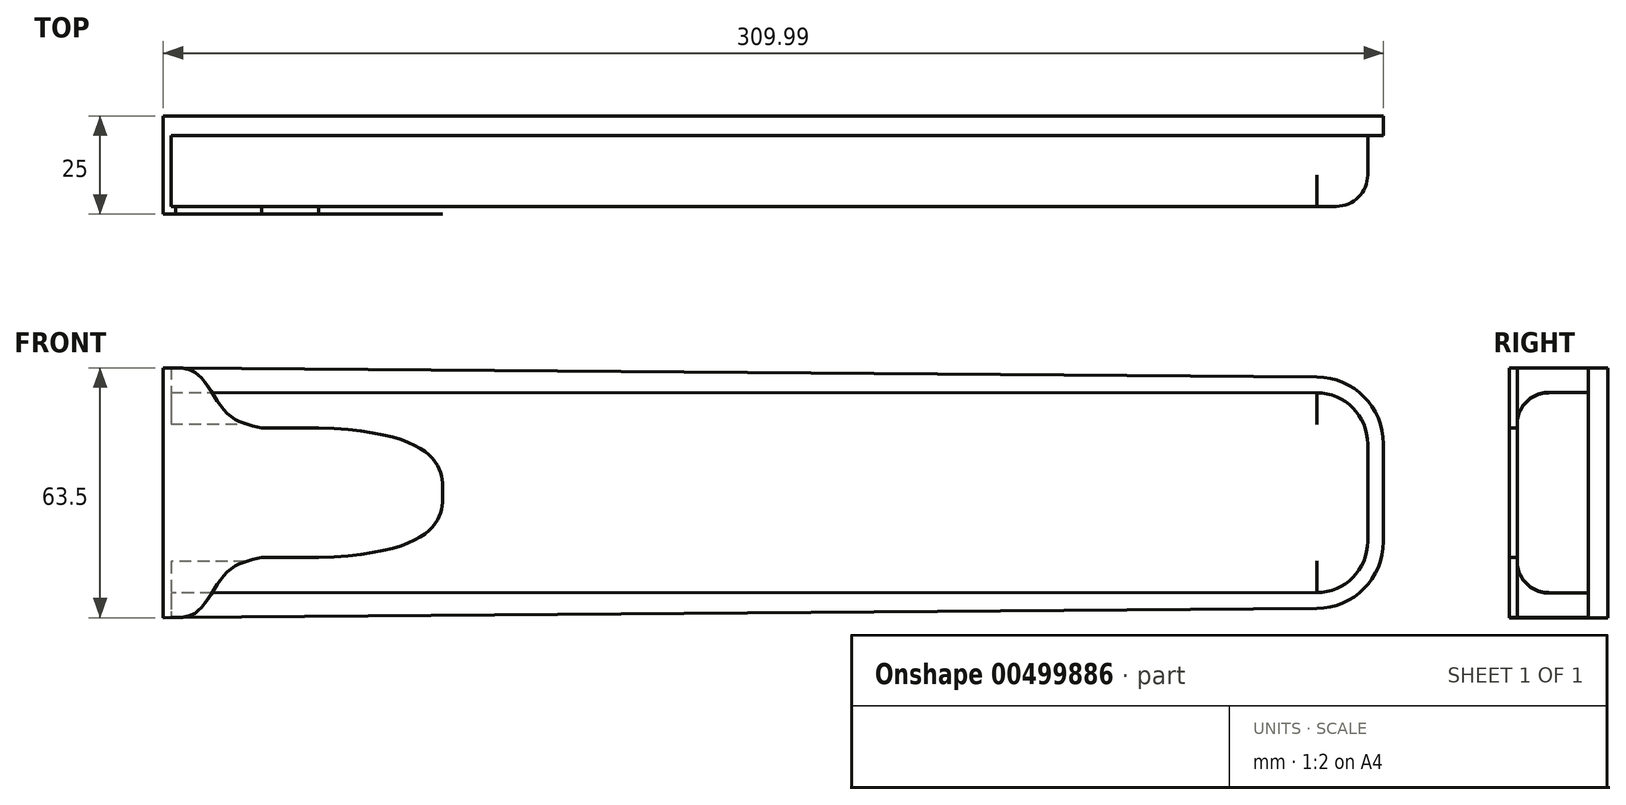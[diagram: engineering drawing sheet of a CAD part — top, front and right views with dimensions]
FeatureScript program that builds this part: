
annotation { "Feature Type Name" : "Feature", "Feature Type Description" : "" }
export const myFeature = defineFeature(function(context is Context, id is Id, definition is map)
    precondition{}
    {
        {
            var Q0;
            Q0=qCreatedBy(makeId("Front.planeOp"),FACE);
            var sketch = newSketch(context, id + "F0", { "sketchPlane" : qUnion([Q0])});
            skPoint(sketch, "E0.middle", {"position": v(0, 0) * mm});
            skLineSegment(sketch, "E1", {"start": v(-136.9, -2.5) * mm, "end": v(156.22, -0.14) * mm});
            skLineSegment(sketch, "E2", {"start": v(173.08, 16.86) * mm, "end": v(173.08, 41.64) * mm});
            skLineSegment(sketch, "E3", {"start": v(156.22, 58.64) * mm, "end": v(-136.9, 61) * mm});
            skLineSegment(sketch, "E4", {"start": v(-136.9, 61) * mm, "end": v(-136.9, -2.5) * mm});
            skPoint(sketch, "E5.visualSharp", {"position": v(173.08, 58.5) * mm});
            skArc(sketch, "E5.filletArc", {"start": v(173.08, 41.64) * mm, "mid": v(168.15, 53.6) * mm, "end": v(156.22, 58.64) * mm});
            skPoint(sketch, "E6.visualSharp", {"position": v(173.08, 0) * mm});
            skArc(sketch, "E6.filletArc", {"start": v(156.22, -0.14) * mm, "mid": v(168.15, 4.9) * mm, "end": v(173.08, 16.86) * mm});
            skSolve(sketch);
        }
        {
            var Q0;
            Q0=makeQuery(id+"F0.imprint","IMPRINT",FACE,{"disambiguationData":[TD([[makeQuery(id+"F0.imprint","IMPRINT",EDGE,{"derivedFrom":sQuery(id+"F0.wireOp",EDGE,"E1")}),1.0]])]});
            extrude(context, id + "F1", {"entities" : qUnion([Q0]), "depth" : 5 * mm});
        }
        {
            var Q0;
            Q0=makeQuery(id+"F1.opExtrude","CAP_FACE",FACE,{"disambiguationData":[OSD([sQuery(id+"F0.wireOp",EDGE,"E1"),sQuery(id+"F0.wireOp",EDGE,"E2"),sQuery(id+"F0.wireOp",EDGE,"E3"),sQuery(id+"F0.wireOp",EDGE,"E4"),sQuery(id+"F0.wireOp",EDGE,"E5.filletArc"),sQuery(id+"F0.wireOp",EDGE,"E6.filletArc")])],"isStart":false});
            var sketch = newSketch(context, id + "F2", { "sketchPlane" : qUnion([Q0])});
            skArc(sketch, "E7.0", {"start": v(169.08, 41.64) * mm, "mid": v(165.3, 50.8) * mm, "end": v(156.18, 54.64) * mm});
            skLineSegment(sketch, "E7.1", {"start": v(169.08, 16.86) * mm, "end": v(169.08, 41.64) * mm});
            skArc(sketch, "E7.2", {"start": v(156.18, 3.86) * mm, "mid": v(165.3, 7.7) * mm, "end": v(169.08, 16.86) * mm});
            skLineSegment(sketch, "E8.0", {"start": v(-134.9, 54.75) * mm, "end": v(-134.9, 3.75) * mm});
            skPoint(sketch, "E9", {"position": v(-134.9, 29.25) * mm});
            skPoint(sketch, "E10", {"position": v(-136.9, 29.25) * mm});
            skLineSegment(sketch, "E11", {"start": v(-134.9, 54.75) * mm, "end": v(156.18, 54.64) * mm});
            skLineSegment(sketch, "E12", {"start": v(156.18, 3.86) * mm, "end": v(-134.9, 3.75) * mm});
            skSolve(sketch);
        }
        {
            var Q0;
            Q0=makeQuery(id+"F2.imprint","IMPRINT",FACE,{"disambiguationData":[TD([[makeQuery(id+"F2.imprint","IMPRINT",EDGE,{"derivedFrom":sQuery(id+"F2.wireOp",EDGE,"E7.0")}),1.0]])]});
            extrude(context, id + "F3", {"entities" : qUnion([Q0]), "operationType" : NewBodyOperationType.ADD, "depth" : 18 * mm});
        }
        {
            var Q0;
            Q0=makeQuery(id+"F3.opExtrude","CAP_EDGE",EDGE,{"disambiguationData":[OSD([sQuery(id+"F2.wireOp",EDGE,"E11")])],"isStart":false});
            var Q1;
            Q1=makeQuery(id+"F3.opExtrude","CAP_EDGE",EDGE,{"disambiguationData":[OSD([sQuery(id+"F2.wireOp",EDGE,"E7.0")])],"isStart":false});
            var Q2;
            Q2=makeQuery(id+"F3.opExtrude","CAP_EDGE",EDGE,{"disambiguationData":[OSD([sQuery(id+"F2.wireOp",EDGE,"E7.1")])],"isStart":false});
            var Q3;
            Q3=makeQuery(id+"F3.opExtrude","CAP_EDGE",EDGE,{"disambiguationData":[OSD([sQuery(id+"F2.wireOp",EDGE,"E7.2")])],"isStart":false});
            var Q4;
            Q4=makeQuery(id+"F3.opExtrude","CAP_EDGE",EDGE,{"disambiguationData":[OSD([sQuery(id+"F2.wireOp",EDGE,"E12")])],"isStart":false});
            fillet(context, id + "F4", {"entities" : qUnion([Q0, Q1, Q2, Q3, Q4]), "radius" : 8 * mm, "tangentPropagation" : true, "allowEdgeOverflow" : false});
        }
        {
            var Q0;
            Q0=makeQuery(id+"F1.opExtrude","CAP_FACE",FACE,{"disambiguationData":[OSD([sQuery(id+"F0.wireOp",EDGE,"E1"),sQuery(id+"F0.wireOp",EDGE,"E2"),sQuery(id+"F0.wireOp",EDGE,"E3"),sQuery(id+"F0.wireOp",EDGE,"E4"),sQuery(id+"F0.wireOp",EDGE,"E5.filletArc"),sQuery(id+"F0.wireOp",EDGE,"E6.filletArc")])],"isStart":false});
            var sketch = newSketch(context, id + "F5", { "sketchPlane" : qUnion([Q0])});
            skLineSegment(sketch, "E13.0", {"start": v(-134.9, 61) * mm, "end": v(-134.9, -2.5) * mm});
            skLineSegment(sketch, "E14", {"start": v(-136.9, -2.5) * mm, "end": v(-134.9, -2.5) * mm});
            skLineSegment(sketch, "E15", {"start": v(-136.9, 61) * mm, "end": v(-134.9, 61) * mm});
            skSolve(sketch);
        }
        {
            var Q0;
            {var subQ0=makeQuery(id+"F1.opExtrude","CAP_EDGE",EDGE,{"disambiguationData":[OSD([sQuery(id+"F0.wireOp",EDGE,"E4")])],"isStart":false});Q0=makeQuery(id+"F5.imprint","IMPRINT",FACE,{"disambiguationData":[TD([[makeQuery(id+"F5.imprint","IMPRINT",EDGE,{"derivedFrom":subQ0}),1.0]])]});}
            extrude(context, id + "F6", {"entities" : qUnion([Q0]), "operationType" : NewBodyOperationType.ADD, "depth" : 20 * mm});
        }
        {
            var Q0;
            Q0=makeQuery(id+"F6.opExtrude","SWEPT_FACE",FACE,{"disambiguationData":[OSD([sQuery(id+"F5.wireOp",EDGE,"E13.0")])]});
            var sketch = newSketch(context, id + "F7", { "sketchPlane" : qUnion([Q0])});
            skLineSegment(sketch, "E16.bottom", {"start": v(-25, -2.48) * mm, "end": v(-23, -2.48) * mm});
            skLineSegment(sketch, "E16.top", {"start": v(-25, 60.98) * mm, "end": v(-23, 60.98) * mm});
            skLineSegment(sketch, "E16.left", {"start": v(-25, -2.48) * mm, "end": v(-25, 60.98) * mm});
            skLineSegment(sketch, "E16.right", {"start": v(-23, -2.48) * mm, "end": v(-23, 60.98) * mm});
            skSolve(sketch);
        }
        {
            var Q0;
            {var subQ3=sQuery(id+"F7.wireOp",EDGE,"E16.bottom");Q0=makeQuery(id+"F7.imprint","IMPRINT",FACE,{"disambiguationData":[TD([[makeQuery(id+"F7.imprint","IMPRINT",EDGE,{"derivedFrom":subQ3}),1.0]])]});}
            extrude(context, id + "F8", {"entities" : qUnion([Q0]), "operationType" : NewBodyOperationType.ADD, "depth" : 69 * mm});
        }
        {
            var Q0;
            Q0=makeQuery(id+"F8.boolean.opBoolean","MERGE",FACE,{"derivedFrom":[makeQuery(id+"F6.opExtrude","CAP_FACE",FACE,{"disambiguationData":[OSD([sQuery(id+"F0.wireOp",EDGE,"E1"),sQuery(id+"F0.wireOp",EDGE,"E3"),sQuery(id+"F0.wireOp",EDGE,"E4"),sQuery(id+"F5.wireOp",EDGE,"E13.0")])],"isStart":false}),makeQuery(id+"F8.opExtrude","SWEPT_FACE",FACE,{"disambiguationData":[OSD([sQuery(id+"F7.wireOp",EDGE,"E16.left")])]})]});
            var sketch = newSketch(context, id + "F9", { "sketchPlane" : qUnion([Q0])});
            skPoint(sketch, "E17", {"position": v(-136.9, 29.25) * mm});
            skPoint(sketch, "E18", {"position": v(-65.9, 29.25) * mm});
            skPoint(sketch, "E19", {"position": v(-111.9, 45.75) * mm});
            skPoint(sketch, "E20", {"position": v(-97.4, 45.75) * mm});
            skPoint(sketch, "E21", {"position": v(-97.4, 12.75) * mm});
            skPoint(sketch, "E22", {"position": v(-111.9, 12.75) * mm});
            skFitSpline(sketch, "E23", {"points": [v(-134.9, 60.98) * mm, v(-128.26, 59.43) * mm, v(-120.69, 49.45) * mm, v(-111.9, 45.75) * mm], "startDerivative": vector(24.78, 0.16) * mm, "endDerivative": vector(28.19, -5.8) * mm});
            skFitSpline(sketch, "E24.MirrorCS", {"points": [v(-134.9, -2.48) * mm, v(-128.26, -0.93) * mm, v(-120.69, 9.05) * mm, v(-111.9, 12.75) * mm], "startDerivative": vector(24.78, -0.16) * mm, "endDerivative": vector(28.19, 5.8) * mm});
            skLineSegment(sketch, "E25", {"start": v(-111.9, 45.75) * mm, "end": v(-97.4, 45.75) * mm});
            skLineSegment(sketch, "E26", {"start": v(-97.4, 12.75) * mm, "end": v(-111.9, 12.75) * mm});
            skFitSpline(sketch, "E27", {"points": [v(-97.4, 45.75) * mm, v(-65.9, 29.25) * mm], "startDerivative": vector(94.5, -3.36) * mm, "endDerivative": vector(0, -17.53) * mm});
            skFitSpline(sketch, "E28.MirrorCS", {"points": [v(-97.4, 12.75) * mm, v(-65.9, 29.25) * mm], "startDerivative": vector(94.5, 3.36) * mm, "endDerivative": vector(0, 17.53) * mm});
            skSolve(sketch);
        }
        {
            var Q0;
            {var subQ1=sQuery(id+"F9.wireOp",EDGE,"E26");Q0=makeQuery(id+"F9.imprint","IMPRINT",FACE,{"disambiguationData":[TD([[makeQuery(id+"F9.imprint","IMPRINT",EDGE,{"derivedFrom":subQ1}),1.0]])]});}
            var Q1;
            {var subQ0=sQuery(id+"F9.wireOp",EDGE,"E25");Q1=makeQuery(id+"F9.imprint","IMPRINT",FACE,{"disambiguationData":[TD([[makeQuery(id+"F9.imprint","IMPRINT",EDGE,{"derivedFrom":subQ0}),1.0]])]});}
            extrude(context, id + "F10", {"entities" : qUnion([Q0, Q1]), "operationType" : NewBodyOperationType.REMOVE, "oppositeDirection" : true, "depth" : 2 * mm});
        }
    });
